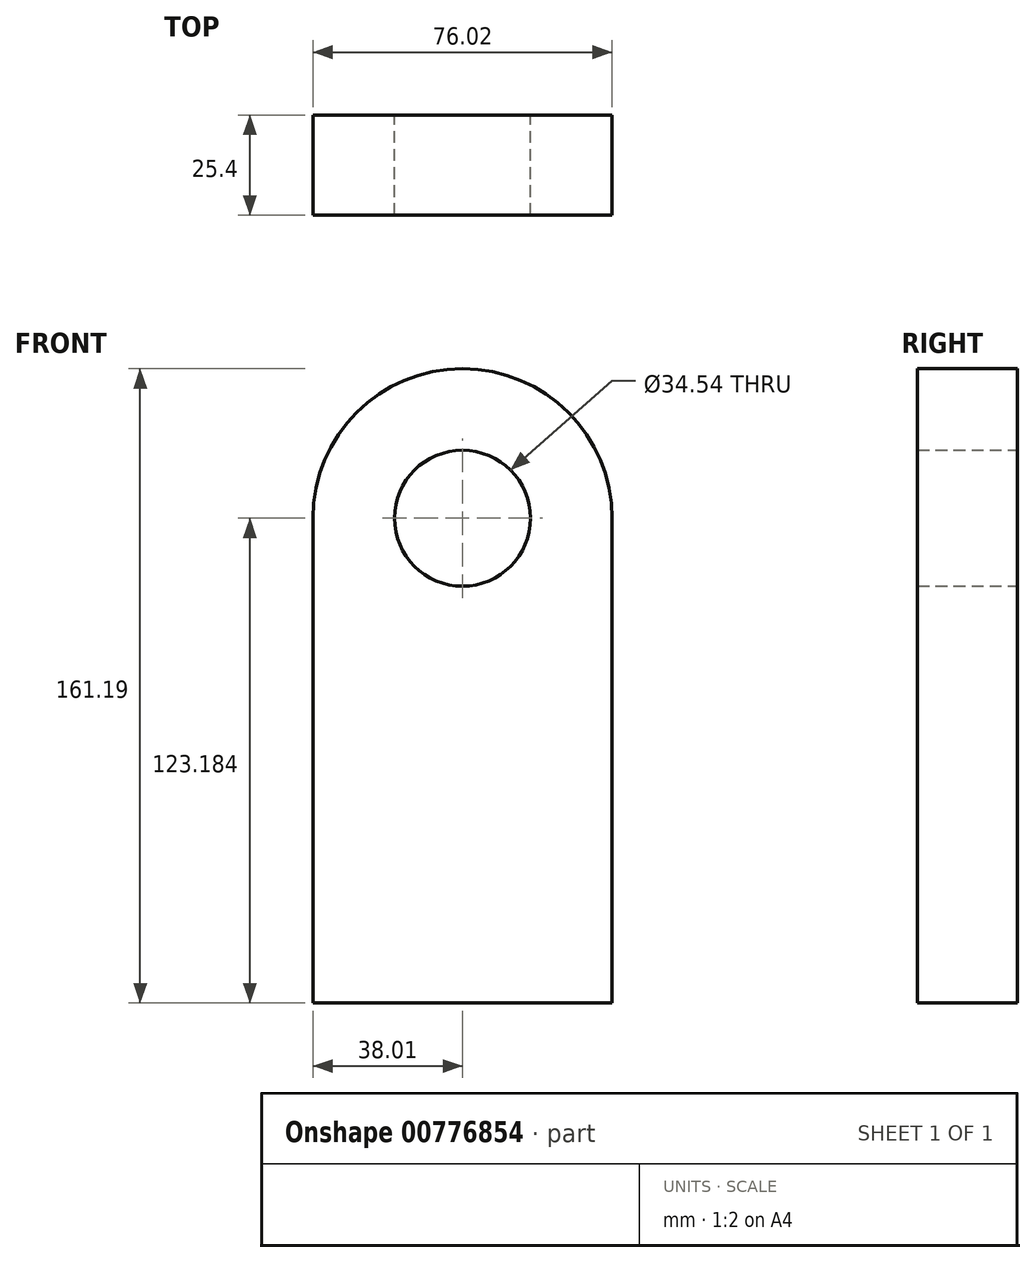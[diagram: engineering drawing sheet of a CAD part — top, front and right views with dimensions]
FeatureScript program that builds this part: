
annotation { "Feature Type Name" : "Feature", "Feature Type Description" : "" }
export const myFeature = defineFeature(function(context is Context, id is Id, definition is map)
    precondition{}
    {
        {
            var Q0;
            Q0=qCreatedBy(makeId("Front.planeOp"),FACE);
            var sketch = newSketch(context, id + "F0", { "sketchPlane" : qUnion([Q0])});
            skLineSegment(sketch, "E0.top", {"start": v(-52.12, -84.67) * mm, "end": v(23.9, -84.67) * mm});
            skLineSegment(sketch, "E0.left", {"start": v(-52.12, 38.51) * mm, "end": v(-52.12, -84.67) * mm});
            skLineSegment(sketch, "E0.right", {"start": v(23.9, 38.51) * mm, "end": v(23.9, -84.67) * mm});
            skPoint(sketch, "E0.middle", {"position": v(-14.1, -23.08) * mm});
            skCircle(sketch, "E1", {"center": v(-14.1, 38.51) * mm, "radius": 17.27 * mm});
            skArc(sketch, "E2", {"start": v(-52.12, 38.51) * mm, "mid": v(-14.1, 76.52) * mm, "end": v(23.9, 38.51) * mm});
            skSolve(sketch);
        }
        {
            var Q0;
            Q0=makeQuery(id+"F0.imprint","IMPRINT",FACE,{"disambiguationData":[TD([[makeQuery(id+"F0.imprint","IMPRINT",EDGE,{"derivedFrom":sQuery(id+"F0.wireOp",EDGE,"E0.top")}),1.0]])]});
            extrude(context, id + "F1", {"entities" : qUnion([Q0]), "depth" : 25.4 * mm, "offsetDistance" : 25.4 * mm});
        }
    });
